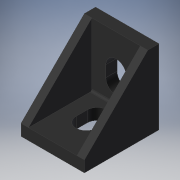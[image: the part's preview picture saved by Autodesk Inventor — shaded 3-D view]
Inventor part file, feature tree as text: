
AUTODESK INVENTOR PART (.ipt)
format: ipt  version: 2025 (Build 290162000, 162)  size: 152,576 bytes
history: native  units: mm
features: extrude x7, sketch x7
ambient origin geometry x8: Origin, YZ Plane, XZ Plane, XY Plane, X Axis, Y Axis, Z Axis, Center Point
bodies: Solid1 (feature_tree)
feature tree (14):
  extrude  "Extrusion1"  Depth=13.0mm TaperAngle=0.0deg
  extrude  "Extrusion2"  Depth=12.0mm TaperAngle=0.0deg
  extrude  "Extrusion3"  Depth=12.0mm TaperAngle=0.0deg
  extrude  "Extrusion4"  [1 undecoded]
  extrude  "Extrusion5"  [1 undecoded]
  extrude  "Extrusion6"  [1 undecoded]
  extrude  "Extrusion7"  [1 undecoded]
  sketch  "Sketch_1"  dims[d0=17.0mm d1=0.0mm d2=13.0mm d3=0.0mm]
  sketch  "Sketch_2"  dims[d4=12.0mm d5=0.0mm d6=12.0mm d7=0.0mm]
  sketch  "Sketch_3"  dims[d8=12.0mm d9=0.0mm d10=5.0mm d11=0.0mm]
  sketch  "Sketch_4"  dims[d12=5.0mm d13=0.0mm]
  sketch  "Sketch_5"
  sketch  "Sketch_10"
  sketch  "Sketch_11"
note: 4 required parameter values undecoded (feature->parameter linkage not recoverable at this tier; creation-order binding heuristic only, values carry confidence <= 0.55)
